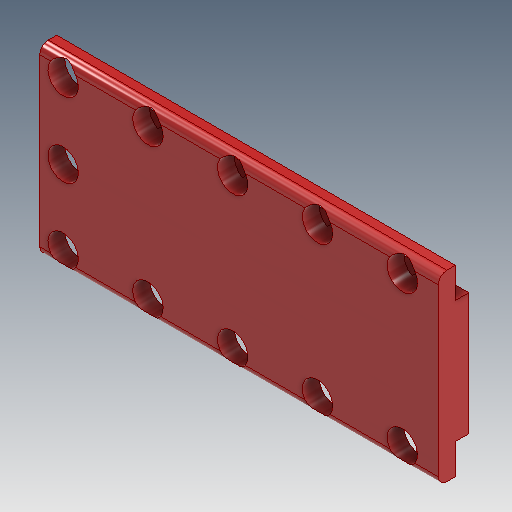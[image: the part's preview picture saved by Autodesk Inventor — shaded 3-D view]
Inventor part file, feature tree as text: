
AUTODESK INVENTOR PART (.ipt)
format: ipt  version: 2020.3 (Build 243373010, 373A)  size: 219,648 bytes
history: native  units: mm
features: sketch x2, extrude x2, hole x2, chamfer x1, fillet x1, pattern_linear x1
ambient origin geometry x8: Origin, YZ Plane, XZ Plane, XY Plane, X Axis, Y Axis, Z Axis, Center Point
bodies: Body1 (feature_tree)
feature tree (9):
  sketch  "Sketch1"  dims[d0=108.0mm d1=235.0mm]
  extrude  "Extrusion2"  Depth=235.0mm
  extrude  "Extrusion3"  Depth=10.0mm
  chamfer  "Chamfer1"  Distance=10.0mm
  fillet  "Fillet1"  Radius=10.0mm
  sketch  "Sketch3"  dims[d4=205.69mm d5=72.0mm d6=10.0mm d7=0.0mm d8=10.0mm d9=0.0mm d10=2.0mm d11=2.0mm d12=45.0deg d13=5.0mm d18=98.0mm d19=108.0mm d20=87.851mm d21=43.9255mm d22=221.210734mm d23=18.0mm d24=12.0mm d25=4.0mm d26=2.0mm d27=90.0deg d28=50.0mm d29=20.594885mm d30=50.0mm d32=50.0mm d33=18.0mm d34=12.0mm d35=4.0mm d36=2.0mm d37=90.0deg d38=15.0mm d39=20.594885mm]
  hole  "Hole1"  [1 undecoded]
  pattern_linear  "Rectangular Pattern1"  Spacing1=5.0mm  [1 undecoded]
  hole  "Hole2"  [1 undecoded]
note: 3 required parameter values undecoded (feature->parameter linkage not recoverable at this tier; creation-order binding heuristic only, values carry confidence <= 0.55)
